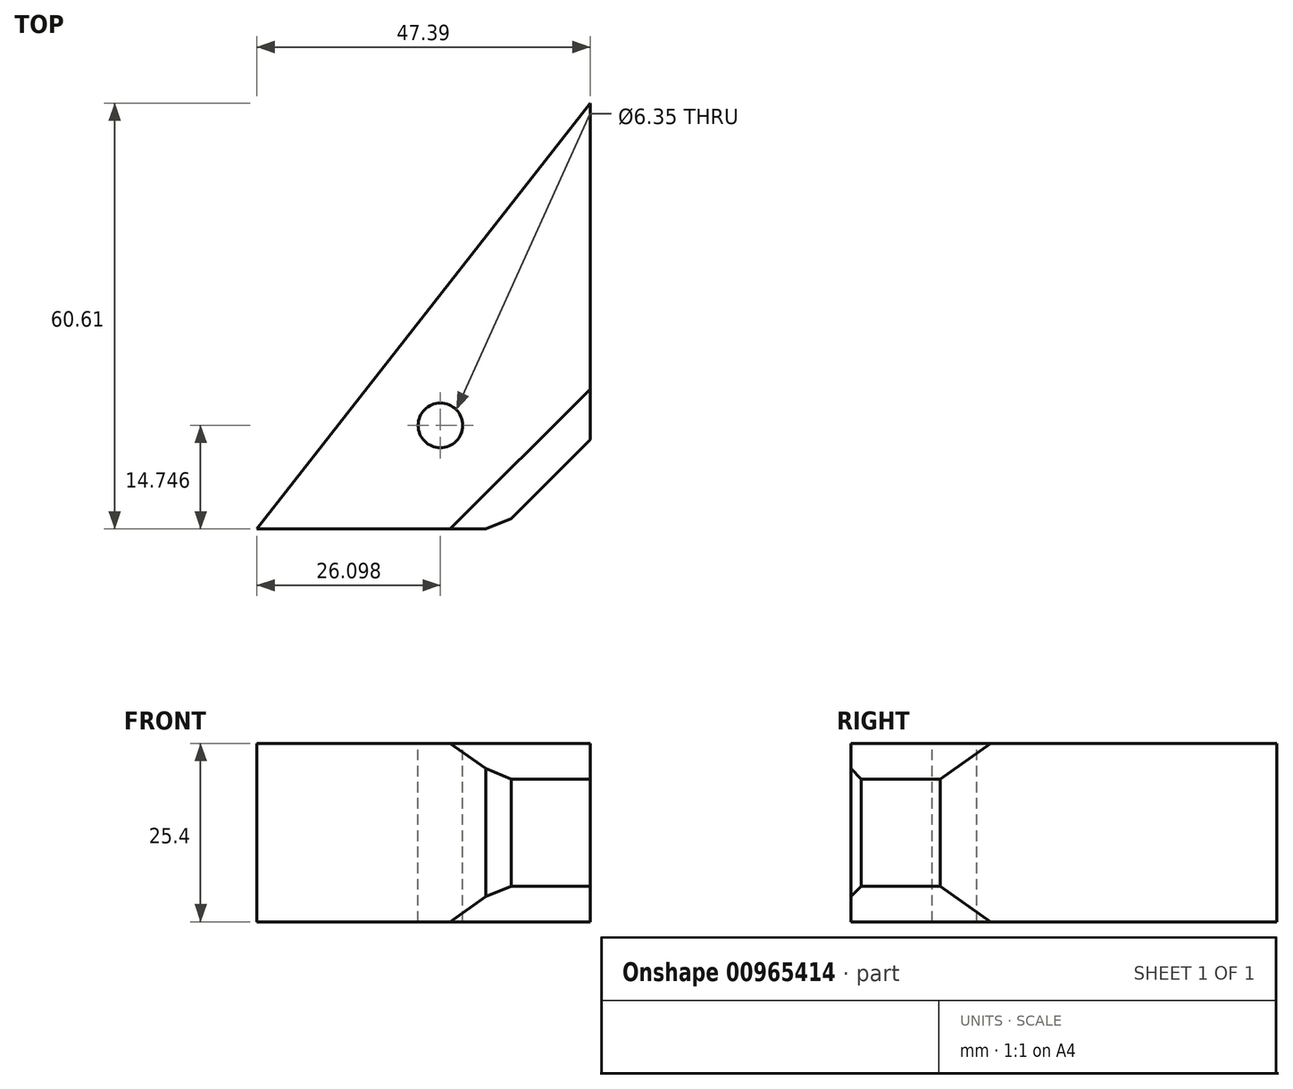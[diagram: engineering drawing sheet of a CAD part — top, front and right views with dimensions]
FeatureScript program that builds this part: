
annotation { "Feature Type Name" : "Feature", "Feature Type Description" : "" }
export const myFeature = defineFeature(function(context is Context, id is Id, definition is map)
    precondition{}
    {
        {
            var Q0;
            Q0=qCreatedBy(makeId("Top.planeOp"),FACE);
            var sketch = newSketch(context, id + "F0", { "sketchPlane" : qUnion([Q0])});
            skLineSegment(sketch, "E0", {"start": v(0, 0) * mm, "end": v(47.39, 60.6) * mm});
            skLineSegment(sketch, "E1", {"start": v(47.39, 60.6) * mm, "end": v(47.39, 0) * mm});
            skLineSegment(sketch, "E2", {"start": v(47.39, 0) * mm, "end": v(0, 0) * mm});
            skSolve(sketch);
        }
        {
            var Q0;
            Q0 = qSketchRegion(id + "F0", true);
            extrude(context, id + "F1", {"entities" : qUnion([Q0]), "depth" : 25.4 * mm, "offsetDistance" : 25.4 * mm});
        }
        {
            var Q0;
            Q0=makeQuery(id+"F1.opExtrude","SWEPT_EDGE",EDGE,{"disambiguationData":[OSD([sQuery(id+"F0.wireOp",EDGE,"E1"),sQuery(id+"F0.wireOp",EDGE,"E2")])]});
            chamfer(context, id + "F2", {"entities" : qUnion([Q0]), "width" : 12.7 * mm, "tangentPropagation" : true});
        }
        {
            var Q0;
            {var subQ0=sQuery(id+"F0.wireOp",EDGE,"E2");var subQ1=sQuery(id+"F0.wireOp",EDGE,"E1");Q0=makeQuery(id+"F2.opChamfer","BLEND_EDGE",EDGE,{"blendedFrom":[makeQuery(id+"F1.opExtrude","SWEPT_EDGE",EDGE,{"disambiguationData":[OSD([subQ1,subQ0])]}),makeQuery(id+"F1.opExtrude","CAP_FACE",FACE,{"disambiguationData":[OSD([sQuery(id+"F0.wireOp",EDGE,"E0"),subQ1,subQ0])],"isStart":false})],"blendedInto":[makeQuery(id+"F1.opExtrude","CAP_FACE",FACE,{"disambiguationData":[OSD([sQuery(id+"F0.wireOp",EDGE,"E0"),subQ1,subQ0])],"isStart":false})]});}
            chamfer(context, id + "F3", {"entities" : qUnion([Q0]), "width" : 5.08 * mm, "tangentPropagation" : true});
        }
        {
            var Q0;
            {var subQ0=sQuery(id+"F0.wireOp",EDGE,"E2");var subQ1=sQuery(id+"F0.wireOp",EDGE,"E1");Q0=makeQuery(id+"F2.opChamfer","BLEND_EDGE",EDGE,{"blendedFrom":[makeQuery(id+"F1.opExtrude","SWEPT_EDGE",EDGE,{"disambiguationData":[OSD([subQ1,subQ0])]}),makeQuery(id+"F1.opExtrude","CAP_FACE",FACE,{"disambiguationData":[OSD([sQuery(id+"F0.wireOp",EDGE,"E0"),subQ1,subQ0])],"isStart":true})],"blendedInto":[makeQuery(id+"F1.opExtrude","CAP_FACE",FACE,{"disambiguationData":[OSD([sQuery(id+"F0.wireOp",EDGE,"E0"),subQ1,subQ0])],"isStart":true})]});}
            chamfer(context, id + "F4", {"entities" : qUnion([Q0]), "width" : 5.08 * mm, "tangentPropagation" : true});
        }
        {
            var Q0;
            {var subQ0=sQuery(id+"F0.wireOp",EDGE,"E2");Q0=makeQuery(id+"F2.opChamfer","BLEND_EDGE",EDGE,{"blendedFrom":[makeQuery(id+"F1.opExtrude","SWEPT_EDGE",EDGE,{"disambiguationData":[OSD([sQuery(id+"F0.wireOp",EDGE,"E1"),subQ0])]}),makeQuery(id+"F1.opExtrude","SWEPT_FACE",FACE,{"disambiguationData":[OSD([subQ0])]})],"blendedInto":[makeQuery(id+"F1.opExtrude","SWEPT_FACE",FACE,{"disambiguationData":[OSD([subQ0])]})]});}
            chamfer(context, id + "F5", {"entities" : qUnion([Q0]), "width" : 5.08 * mm, "tangentPropagation" : true});
        }
        {
            var Q0;
            Q0=makeQuery(id+"F1.opExtrude","CAP_FACE",FACE,{"disambiguationData":[OSD([sQuery(id+"F0.wireOp",EDGE,"E0"),sQuery(id+"F0.wireOp",EDGE,"E1"),sQuery(id+"F0.wireOp",EDGE,"E2")])],"isStart":false});
            var sketch = newSketch(context, id + "F6", { "sketchPlane" : qUnion([Q0])});
            skPoint(sketch, "E3", {"position": v(26.1, 14.75) * mm});
            skSolve(sketch);
        }
        {
            var Q0;
            Q0=sQuery(id+"F6.wireOp",VERTEX,"E3");
            var Q1;
            Q1=makeQuery(id+"F1.opExtrude","SWEPT_BODY",BODY,{"disambiguationData":[OSD([sQuery(id+"F0.wireOp",EDGE,"E0"),sQuery(id+"F0.wireOp",EDGE,"E1"),sQuery(id+"F0.wireOp",EDGE,"E2")])]});
            hole(context, id + "F7", {"style" : HoleStyle.SIMPLE, "endStyle" : HoleEndStyle.THROUGH, "holeDiameter" : 6.35 * mm, "majorDiameter" : 6.35 * mm, "isTappedThrough" : true, "tappedDepth" : 12.7 * mm, "tapClearance" : 3, "locations" : qUnion([Q0]), "scope" : qUnion([Q1])});
        }
    });
